FCSTD DOCUMENT  (FreeCAD 0.22R38261 (Git))
Label: ящик на стену
License: All rights reserved
LicenseURL: https://en.wikipedia.org/wiki/All_rights_reserved
objects: Sketcher::SketchObject×1, PartDesign::Body×1, App::Part×1
note: 2 computed .brp shape members not serialized (recipe doc carries the construction recipe); baked Part::Feature solids carry a one-line shape summary decoded from their .brp

FEATURE [Sketcher::SketchObject] Sketch
  AttachmentSupport = -> [XY_Plane001]
  FullyConstrained = false
  MapMode = 5
  sketch-geometry (12):
    g0: LineSegment StartX=0 StartY=0 StartZ=0 EndX=220 EndY=0 EndZ=0
    g1: LineSegment StartX=0 StartY=0 StartZ=0 EndX=0 EndY=80 EndZ=0
    g2: LineSegment StartX=220 StartY=0 StartZ=0 EndX=220 EndY=80 EndZ=0
    g3: ArcOfCircle CenterX=110 CenterY=-121.867 CenterZ=0 NormalX=0 NormalY=0 NormalZ=1 AngleXU=0 Radius=229.892 StartAngle=1.07187 EndAngle=2.06973
    g4: LineSegment StartX=3 StartY=4 StartZ=0 EndX=217 EndY=4 EndZ=0
    g5: LineSegment StartX=3 StartY=4 StartZ=0 EndX=3 EndY=78 EndZ=0
    g6: LineSegment StartX=217 StartY=4 StartZ=0 EndX=217 EndY=78 EndZ=0
    g7: ArcOfCircle CenterX=110 CenterY=-112.252 CenterZ=0 NormalX=0 NormalY=0 NormalZ=1 AngleXU=0 Radius=218.277 StartAngle=1.05847 EndAngle=2.08312
    g8: LineSegment StartX=3 StartY=78 StartZ=0 EndX=110 EndY=106.025 EndZ=0
    g9: LineSegment StartX=110 StartY=106.025 StartZ=0 EndX=217 EndY=78 EndZ=0
    g10: LineSegment StartX=0 StartY=80 StartZ=0 EndX=110 EndY=108.025 EndZ=0
    g11: LineSegment StartX=110 StartY=108.025 StartZ=0 EndX=220 EndY=80 EndZ=0
  constraints (34):
    c: Coincident(g0,g-1)
    c: PointOnObject(g0,g-1)
    c: DistanceX(g0,g0) = 220
    c: Coincident(g1,g0)
    c: PointOnObject(g1,g-2)
    c: DistanceY(g1,g1) = 80
    c: Coincident(g2,g0)
    c: Vertical(g2)
    c: Equal(g1,g2)
    c: Coincident(g3,g1)
    c: Coincident(g3,g2)
    c: Horizontal(g4)
    c: DistanceY(g0,g4) = 4
    c: DistanceX(g4,g0) = 3
    c: DistanceX(g0,g4) = 3
    c: Coincident(g5,g4)
    c: Vertical(g5)
    c: DistanceY(g5,g1) = 2
    c: Coincident(g6,g4)
    c: Vertical(g6)
    c: Equal(g6,g5)
    c: Coincident(g7,g5)
    c: Coincident(g7,g6)
    c: Coincident(g8,g5)
    c: PointOnObject(g8,g7)
    c: Coincident(g9,g8)
    c: Coincident(g9,g6)
    c: Equal(g8,g9)
    c: Coincident(g10,g1)
    c: PointOnObject(g10,g3)
    c: Coincident(g11,g10)
    c: Coincident(g11,g2)
    c: Equal(g10,g11)
    c: DistanceY(g8,g10) = 2
FEATURE [PartDesign::Body] Body
  AllowCompound = false
  Group = -> [Sketch]
  Origin = -> Origin001
FEATURE [App::Part] Part
  Group = -> [Body]
  Origin = -> Origin
